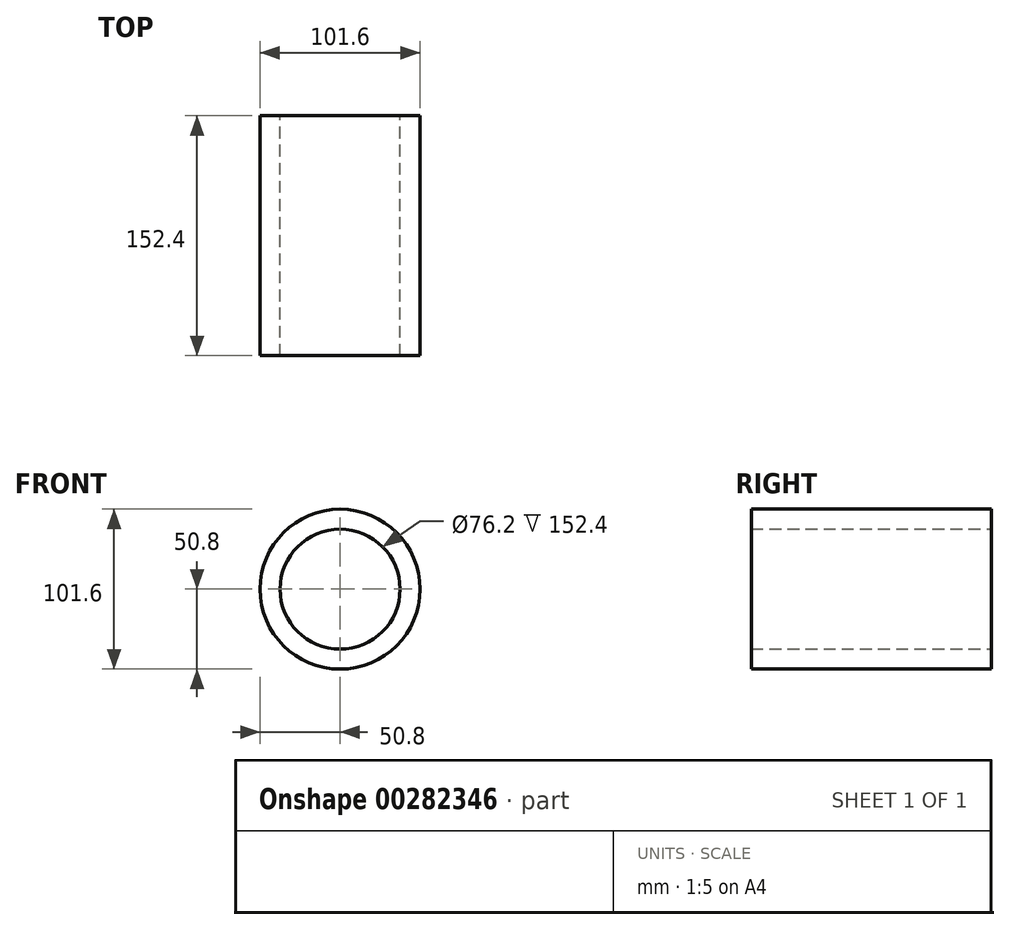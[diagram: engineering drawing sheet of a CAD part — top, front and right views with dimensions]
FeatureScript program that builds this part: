
annotation { "Feature Type Name" : "Feature", "Feature Type Description" : "" }
export const myFeature = defineFeature(function(context is Context, id is Id, definition is map)
    precondition{}
    {
        {
            var Q0;
            Q0=qCreatedBy(makeId("Front.planeOp"),FACE);
            var sketch = newSketch(context, id + "F0", { "sketchPlane" : qUnion([Q0])});
            skCircle(sketch, "E0", {"center": v(0, 0) * mm, "radius": 50.8 * mm});
            skCircle(sketch, "E1", {"center": v(0, 0) * mm, "radius": 38.1 * mm});
            skSolve(sketch);
        }
        {
            var Q0;
            Q0 = qSketchRegion(id + "F0", true);
            extrude(context, id + "F1", {"entities" : qUnion([Q0]), "depth" : 152.4 * mm});
        }
    });
